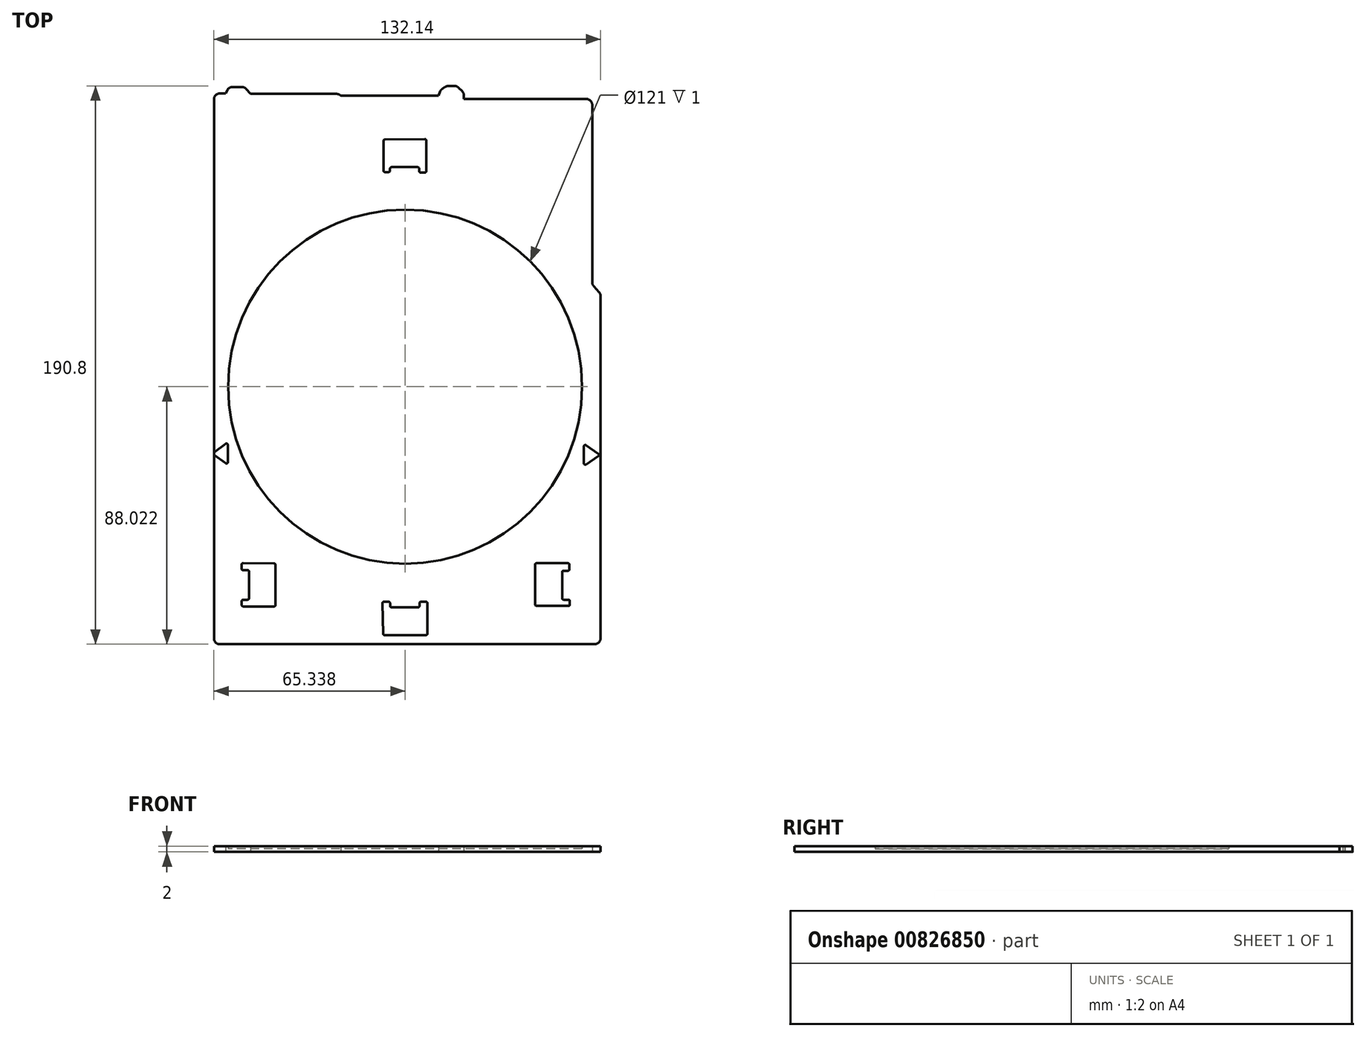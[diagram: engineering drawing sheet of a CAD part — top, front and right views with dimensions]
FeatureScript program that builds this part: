
annotation { "Feature Type Name" : "Feature", "Feature Type Description" : "" }
export const myFeature = defineFeature(function(context is Context, id is Id, definition is map)
    precondition{}
    {
        {
            var Q0;
            Q0=qCreatedBy(makeId("Top.planeOp"),FACE);
            var sketch = newSketch(context, id + "F0", { "sketchPlane" : qUnion([Q0])});
            skCircle(sketch, "E0", {"center": v(8.35, 24.71) * mm, "radius": 60.5 * mm, "construction": true});
            skLineSegment(sketch, "E1", {"start": v(-54.99, 124.93) * mm, "end": v(-53.03, 124.93) * mm});
            skLineSegment(sketch, "E2", {"start": v(-53.03, 124.93) * mm, "end": v(-52.4, 126.1) * mm});
            skLineSegment(sketch, "E3", {"start": v(-50.64, 127.15) * mm, "end": v(-47.47, 127.15) * mm});
            skLineSegment(sketch, "E4", {"start": v(-45.95, 126.45) * mm, "end": v(-44.5, 124.76) * mm});
            skLineSegment(sketch, "E5", {"start": v(-44.5, 124.76) * mm, "end": v(-15.05, 124.76) * mm});
            skLineSegment(sketch, "E6", {"start": v(-13.78, 124.3) * mm, "end": v(-13.6, 124.17) * mm});
            skLineSegment(sketch, "E7", {"start": v(-13.6, 124.17) * mm, "end": v(19.8, 124.17) * mm});
            skLineSegment(sketch, "E8", {"start": v(19.8, 124.17) * mm, "end": v(20.34, 125.59) * mm});
            skLineSegment(sketch, "E9", {"start": v(21.14, 126.57) * mm, "end": v(22.08, 127.18) * mm});
            skLineSegment(sketch, "E10", {"start": v(23.16, 127.5) * mm, "end": v(25.23, 127.5) * mm});
            skLineSegment(sketch, "E11", {"start": v(26.66, 126.9) * mm, "end": v(27.88, 125.64) * mm});
            skLineSegment(sketch, "E12", {"start": v(28.46, 124.24) * mm, "end": v(28.46, 123.02) * mm});
            skLineSegment(sketch, "E13", {"start": v(28.46, 123.02) * mm, "end": v(70.31, 123.02) * mm});
            skLineSegment(sketch, "E14", {"start": v(72.31, 121.02) * mm, "end": v(72.31, 60.41) * mm});
            skLineSegment(sketch, "E15", {"start": v(72.83, 59.08) * mm, "end": v(74.64, 57.06) * mm});
            skLineSegment(sketch, "E16", {"start": v(75.15, 55.72) * mm, "end": v(75.15, -61.3) * mm});
            skLineSegment(sketch, "E17", {"start": v(73.15, -63.3) * mm, "end": v(-54.99, -63.3) * mm});
            skLineSegment(sketch, "E18", {"start": v(-56.99, -61.3) * mm, "end": v(-56.99, 122.93) * mm});
            skPoint(sketch, "E19.visualSharp", {"position": v(-56.99, 124.93) * mm});
            skArc(sketch, "E19.filletArc", {"start": v(-54.99, 124.93) * mm, "mid": v(-56.4, 124.35) * mm, "end": v(-56.99, 122.93) * mm});
            skPoint(sketch, "E20.visualSharp", {"position": v(72.31, 123.02) * mm});
            skArc(sketch, "E20.filletArc", {"start": v(72.31, 121.02) * mm, "mid": v(71.73, 122.43) * mm, "end": v(70.31, 123.02) * mm});
            skPoint(sketch, "E21.visualSharp", {"position": v(-51.83, 127.15) * mm});
            skArc(sketch, "E21.filletArc", {"start": v(-50.64, 127.15) * mm, "mid": v(-51.67, 126.87) * mm, "end": v(-52.4, 126.1) * mm});
            skPoint(sketch, "E22.visualSharp", {"position": v(-46.55, 127.15) * mm});
            skArc(sketch, "E22.filletArc", {"start": v(-45.95, 126.45) * mm, "mid": v(-46.63, 126.97) * mm, "end": v(-47.47, 127.15) * mm});
            skPoint(sketch, "E23.visualSharp", {"position": v(22.58, 127.5) * mm});
            skArc(sketch, "E23.filletArc", {"start": v(23.16, 127.5) * mm, "mid": v(22.6, 127.41) * mm, "end": v(22.08, 127.18) * mm});
            skPoint(sketch, "E24.visualSharp", {"position": v(20.57, 126.21) * mm});
            skArc(sketch, "E24.filletArc", {"start": v(21.14, 126.57) * mm, "mid": v(20.66, 126.14) * mm, "end": v(20.34, 125.59) * mm});
            skPoint(sketch, "E25.visualSharp", {"position": v(26.07, 127.5) * mm});
            skArc(sketch, "E25.filletArc", {"start": v(26.66, 126.9) * mm, "mid": v(26, 127.33) * mm, "end": v(25.23, 127.5) * mm});
            skPoint(sketch, "E26.visualSharp", {"position": v(28.46, 125.06) * mm});
            skArc(sketch, "E26.filletArc", {"start": v(28.46, 124.24) * mm, "mid": v(28.3, 125) * mm, "end": v(27.88, 125.64) * mm});
            skPoint(sketch, "E27.visualSharp", {"position": v(75.15, 56.49) * mm});
            skArc(sketch, "E27.filletArc", {"start": v(75.15, 55.72) * mm, "mid": v(75.02, 56.44) * mm, "end": v(74.64, 57.06) * mm});
            skPoint(sketch, "E28.visualSharp", {"position": v(72.31, 59.65) * mm});
            skArc(sketch, "E28.filletArc", {"start": v(72.31, 60.41) * mm, "mid": v(72.45, 59.7) * mm, "end": v(72.83, 59.08) * mm});
            skPoint(sketch, "E29.visualSharp", {"position": v(-14.33, 124.76) * mm});
            skArc(sketch, "E29.filletArc", {"start": v(-13.78, 124.3) * mm, "mid": v(-14.37, 124.65) * mm, "end": v(-15.05, 124.76) * mm});
            skPoint(sketch, "E30.visualSharp", {"position": v(75.15, -63.3) * mm});
            skArc(sketch, "E30.filletArc", {"start": v(73.15, -63.3) * mm, "mid": v(74.57, -62.72) * mm, "end": v(75.15, -61.3) * mm});
            skPoint(sketch, "E31.visualSharp", {"position": v(-56.99, -63.3) * mm});
            skArc(sketch, "E31.filletArc", {"start": v(-56.99, -61.3) * mm, "mid": v(-56.4, -62.72) * mm, "end": v(-54.99, -63.3) * mm});
            skSolve(sketch);
        }
        {
            var Q0;
            Q0 = qSketchRegion(id + "F0", true);
            extrude(context, id + "F1", {"entities" : qUnion([Q0]), "depth" : 1 * mm, "offsetDistance" : 25 * mm});
        }
        {
            var Q0;
            Q0=makeQuery(id+"F1.opExtrude","CAP_FACE",FACE,{"disambiguationData":[OSD([sQuery(id+"F0.wireOp",EDGE,"E1"),sQuery(id+"F0.wireOp",EDGE,"E2"),sQuery(id+"F0.wireOp",EDGE,"E3"),sQuery(id+"F0.wireOp",EDGE,"E4"),sQuery(id+"F0.wireOp",EDGE,"E5"),sQuery(id+"F0.wireOp",EDGE,"E6"),sQuery(id+"F0.wireOp",EDGE,"E7"),sQuery(id+"F0.wireOp",EDGE,"E8"),sQuery(id+"F0.wireOp",EDGE,"E9"),sQuery(id+"F0.wireOp",EDGE,"E10"),sQuery(id+"F0.wireOp",EDGE,"E11"),sQuery(id+"F0.wireOp",EDGE,"E12"),sQuery(id+"F0.wireOp",EDGE,"E13"),sQuery(id+"F0.wireOp",EDGE,"E14"),sQuery(id+"F0.wireOp",EDGE,"E15"),sQuery(id+"F0.wireOp",EDGE,"E16"),sQuery(id+"F0.wireOp",EDGE,"E17"),sQuery(id+"F0.wireOp",EDGE,"E18"),sQuery(id+"F0.wireOp",EDGE,"E19.filletArc"),sQuery(id+"F0.wireOp",EDGE,"E20.filletArc"),sQuery(id+"F0.wireOp",EDGE,"E21.filletArc"),sQuery(id+"F0.wireOp",EDGE,"E22.filletArc"),sQuery(id+"F0.wireOp",EDGE,"E23.filletArc"),sQuery(id+"F0.wireOp",EDGE,"E24.filletArc"),sQuery(id+"F0.wireOp",EDGE,"E25.filletArc"),sQuery(id+"F0.wireOp",EDGE,"E26.filletArc"),sQuery(id+"F0.wireOp",EDGE,"E27.filletArc"),sQuery(id+"F0.wireOp",EDGE,"E28.filletArc"),sQuery(id+"F0.wireOp",EDGE,"E29.filletArc"),sQuery(id+"F0.wireOp",EDGE,"E30.filletArc"),sQuery(id+"F0.wireOp",EDGE,"E31.filletArc")])],"isStart":false});
            var sketch = newSketch(context, id + "F2", { "sketchPlane" : qUnion([Q0])});
            skLineSegment(sketch, "E32.0", {"start": v(-44.5, 124.76) * mm, "end": v(-15.05, 124.76) * mm});
            skLineSegment(sketch, "E32.1", {"start": v(75.15, 55.72) * mm, "end": v(75.15, -61.3) * mm});
            skLineSegment(sketch, "E32.2", {"start": v(-56.99, -61.3) * mm, "end": v(-56.99, 122.93) * mm});
            skLineSegment(sketch, "E32.3", {"start": v(28.46, 123.02) * mm, "end": v(70.31, 123.02) * mm});
            skLineSegment(sketch, "E32.4", {"start": v(73.15, -63.3) * mm, "end": v(-54.99, -63.3) * mm});
            skLineSegment(sketch, "E32.5", {"start": v(-13.6, 124.17) * mm, "end": v(19.8, 124.17) * mm});
            skLineSegment(sketch, "E32.6", {"start": v(72.31, 121.02) * mm, "end": v(72.31, 60.41) * mm});
            skCircle(sketch, "E32.7", {"center": v(8.35, 24.71) * mm, "radius": 60.5 * mm});
            skLineSegment(sketch, "E32.8", {"start": v(-56.99, -61.3) * mm, "end": v(-56.99, 122.93) * mm});
            skLineSegment(sketch, "E32.9", {"start": v(72.31, 121.02) * mm, "end": v(72.31, 60.41) * mm});
            skLineSegment(sketch, "E33.0", {"start": v(-50.64, 127.15) * mm, "end": v(-47.47, 127.15) * mm});
            skLineSegment(sketch, "E33.1", {"start": v(-45.95, 126.45) * mm, "end": v(-44.5, 124.76) * mm});
            skArc(sketch, "E33.2", {"start": v(-54.99, 124.93) * mm, "mid": v(-56.4, 124.35) * mm, "end": v(-56.99, 122.93) * mm});
            skLineSegment(sketch, "E33.3", {"start": v(-54.99, 124.93) * mm, "end": v(-53.03, 124.93) * mm});
            skArc(sketch, "E33.4", {"start": v(-50.64, 127.15) * mm, "mid": v(-51.67, 126.87) * mm, "end": v(-52.4, 126.1) * mm});
            skLineSegment(sketch, "E34.0", {"start": v(28.46, 124.24) * mm, "end": v(28.46, 123.02) * mm});
            skLineSegment(sketch, "E34.1", {"start": v(19.8, 124.17) * mm, "end": v(20.34, 125.59) * mm});
            skLineSegment(sketch, "E34.2", {"start": v(23.16, 127.5) * mm, "end": v(25.23, 127.5) * mm});
            skLineSegment(sketch, "E34.3", {"start": v(26.66, 126.9) * mm, "end": v(27.88, 125.64) * mm});
            skArc(sketch, "E34.4", {"start": v(21.14, 126.57) * mm, "mid": v(20.66, 126.14) * mm, "end": v(20.34, 125.59) * mm});
            skArc(sketch, "E34.5", {"start": v(26.66, 126.9) * mm, "mid": v(26, 127.33) * mm, "end": v(25.23, 127.5) * mm});
            skArc(sketch, "E34.6", {"start": v(28.46, 124.24) * mm, "mid": v(28.3, 125) * mm, "end": v(27.88, 125.64) * mm});
            skArc(sketch, "E35.0", {"start": v(72.31, 121.02) * mm, "mid": v(71.73, 122.43) * mm, "end": v(70.31, 123.02) * mm});
            skSolve(sketch);
        }
        {
            var Q0;
            Q0=makeQuery(id+"F2.imprint","IMPRINT",FACE,{"disambiguationData":[TD([[makeQuery(id+"F2.imprint","IMPRINT",EDGE,{"derivedFrom":sQuery(id+"F2.wireOp",EDGE,"E32.0")}),-1.0]])]});
            extrude(context, id + "F3", {"entities" : qUnion([Q0]), "operationType" : NewBodyOperationType.ADD, "depth" : 1 * mm, "offsetDistance" : 25 * mm});
        }
        {
            var Q0;
            Q0=makeQuery(id+"F3.opExtrude","CAP_FACE",FACE,{"disambiguationData":[OSD([sQuery(id+"F0.wireOp",EDGE,"E2"),sQuery(id+"F0.wireOp",EDGE,"E6"),sQuery(id+"F0.wireOp",EDGE,"E9"),sQuery(id+"F0.wireOp",EDGE,"E15"),sQuery(id+"F0.wireOp",EDGE,"E22.filletArc"),sQuery(id+"F0.wireOp",EDGE,"E23.filletArc"),sQuery(id+"F0.wireOp",EDGE,"E27.filletArc"),sQuery(id+"F0.wireOp",EDGE,"E28.filletArc"),sQuery(id+"F0.wireOp",EDGE,"E29.filletArc"),sQuery(id+"F0.wireOp",EDGE,"E30.filletArc"),sQuery(id+"F0.wireOp",EDGE,"E31.filletArc"),sQuery(id+"F2.wireOp",EDGE,"E32.0"),sQuery(id+"F2.wireOp",EDGE,"E32.1"),sQuery(id+"F2.wireOp",EDGE,"E32.3"),sQuery(id+"F2.wireOp",EDGE,"E32.4"),sQuery(id+"F2.wireOp",EDGE,"E32.5"),sQuery(id+"F2.wireOp",EDGE,"E32.7"),sQuery(id+"F2.wireOp",EDGE,"E32.8"),sQuery(id+"F2.wireOp",EDGE,"E32.9"),sQuery(id+"F2.wireOp",EDGE,"E33.0"),sQuery(id+"F2.wireOp",EDGE,"E33.1"),sQuery(id+"F2.wireOp",EDGE,"E33.2"),sQuery(id+"F2.wireOp",EDGE,"E33.3"),sQuery(id+"F2.wireOp",EDGE,"E33.4"),sQuery(id+"F2.wireOp",EDGE,"E34.0"),sQuery(id+"F2.wireOp",EDGE,"E34.1"),sQuery(id+"F2.wireOp",EDGE,"E34.2"),sQuery(id+"F2.wireOp",EDGE,"E34.3"),sQuery(id+"F2.wireOp",EDGE,"E34.4"),sQuery(id+"F2.wireOp",EDGE,"E34.5"),sQuery(id+"F2.wireOp",EDGE,"E34.6"),sQuery(id+"F2.wireOp",EDGE,"E35.0")])],"isStart":false});
            var sketch = newSketch(context, id + "F4", { "sketchPlane" : qUnion([Q0])});
            skLineSegment(sketch, "E36", {"start": v(-47.55, -36.14) * mm, "end": v(-47.55, -37.5) * mm});
            skLineSegment(sketch, "E37", {"start": v(-47.05, -38) * mm, "end": v(-45.5, -38) * mm});
            skLineSegment(sketch, "E38", {"start": v(-45, -38.5) * mm, "end": v(-45, -47.6) * mm});
            skLineSegment(sketch, "E39", {"start": v(-45.5, -48.1) * mm, "end": v(-47, -48.1) * mm});
            skLineSegment(sketch, "E40", {"start": v(-47.5, -48.6) * mm, "end": v(-47.5, -49.9) * mm});
            skLineSegment(sketch, "E41", {"start": v(-47, -50.4) * mm, "end": v(-36.45, -50.4) * mm});
            skLineSegment(sketch, "E42", {"start": v(-35.95, -49.9) * mm, "end": v(-35.95, -36.22) * mm});
            skLineSegment(sketch, "E43", {"start": v(-36.44, -35.72) * mm, "end": v(-47.05, -35.64) * mm});
            skLineSegment(sketch, "E44", {"start": v(1.1, -48.8) * mm, "end": v(2.72, -48.8) * mm});
            skLineSegment(sketch, "E45", {"start": v(3.22, -49.3) * mm, "end": v(3.22, -50.21) * mm});
            skLineSegment(sketch, "E46", {"start": v(3.72, -50.71) * mm, "end": v(12.76, -50.71) * mm});
            skLineSegment(sketch, "E47", {"start": v(13.26, -50.21) * mm, "end": v(13.26, -49.3) * mm});
            skLineSegment(sketch, "E48", {"start": v(13.76, -48.8) * mm, "end": v(15.47, -48.8) * mm});
            skLineSegment(sketch, "E49", {"start": v(15.97, -49.3) * mm, "end": v(15.97, -59.7) * mm});
            skLineSegment(sketch, "E50", {"start": v(15.47, -60.2) * mm, "end": v(1.31, -60.2) * mm});
            skLineSegment(sketch, "E51", {"start": v(0.82, -59.7) * mm, "end": v(0.6, -49.3) * mm});
            skLineSegment(sketch, "E52", {"start": v(52.8, -36.13) * mm, "end": v(52.8, -49.73) * mm});
            skLineSegment(sketch, "E53", {"start": v(53.3, -50.23) * mm, "end": v(64.17, -50.23) * mm});
            skLineSegment(sketch, "E54", {"start": v(64.67, -49.73) * mm, "end": v(64.67, -48.6) * mm});
            skLineSegment(sketch, "E55", {"start": v(64.17, -48.1) * mm, "end": v(62.55, -48.1) * mm});
            skLineSegment(sketch, "E56", {"start": v(62.05, -47.6) * mm, "end": v(62.05, -38.7) * mm});
            skLineSegment(sketch, "E57", {"start": v(62.55, -38.2) * mm, "end": v(64.02, -38.2) * mm});
            skLineSegment(sketch, "E58", {"start": v(64.52, -37.7) * mm, "end": v(64.52, -36.13) * mm});
            skLineSegment(sketch, "E59", {"start": v(64.02, -35.63) * mm, "end": v(53.3, -35.63) * mm});
            skLineSegment(sketch, "E60", {"start": v(69.46, 4.28) * mm, "end": v(69.46, -1.48) * mm});
            skLineSegment(sketch, "E61", {"start": v(70.24, -1.9) * mm, "end": v(74.42, 0.95) * mm});
            skLineSegment(sketch, "E62", {"start": v(74.42, 1.77) * mm, "end": v(70.25, 4.69) * mm});
            skLineSegment(sketch, "E63", {"start": v(-56.95, 2.2) * mm, "end": v(-53.04, 5.19) * mm});
            skLineSegment(sketch, "E64", {"start": v(-52.24, 4.79) * mm, "end": v(-52.24, -1.08) * mm});
            skLineSegment(sketch, "E65", {"start": v(-53.04, -1.48) * mm, "end": v(-56.95, 1.4) * mm});
            skLineSegment(sketch, "E66", {"start": v(0.97, 108.72) * mm, "end": v(0.97, 98.56) * mm});
            skLineSegment(sketch, "E67", {"start": v(1.47, 98.06) * mm, "end": v(2.7, 98.06) * mm});
            skLineSegment(sketch, "E68", {"start": v(3.2, 98.56) * mm, "end": v(3.2, 99.23) * mm});
            skLineSegment(sketch, "E69", {"start": v(3.7, 99.73) * mm, "end": v(12.67, 99.73) * mm});
            skLineSegment(sketch, "E70", {"start": v(13.17, 99.23) * mm, "end": v(13.17, 98.4) * mm});
            skLineSegment(sketch, "E71", {"start": v(13.67, 97.9) * mm, "end": v(15.14, 97.9) * mm});
            skLineSegment(sketch, "E72", {"start": v(15.64, 98.4) * mm, "end": v(15.64, 108.8) * mm});
            skLineSegment(sketch, "E73", {"start": v(15.14, 109.3) * mm, "end": v(1.47, 109.22) * mm});
            skPoint(sketch, "E74.visualSharp", {"position": v(0.97, 109.22) * mm});
            skArc(sketch, "E74.filletArc", {"start": v(1.47, 109.22) * mm, "mid": v(1.11, 109.08) * mm, "end": v(0.97, 108.72) * mm});
            skPoint(sketch, "E75.visualSharp", {"position": v(15.64, 109.3) * mm});
            skArc(sketch, "E75.filletArc", {"start": v(15.64, 108.8) * mm, "mid": v(15.5, 109.15) * mm, "end": v(15.14, 109.3) * mm});
            skPoint(sketch, "E76.visualSharp", {"position": v(15.64, 97.9) * mm});
            skArc(sketch, "E76.filletArc", {"start": v(15.14, 97.9) * mm, "mid": v(15.5, 98.05) * mm, "end": v(15.64, 98.4) * mm});
            skPoint(sketch, "E77.visualSharp", {"position": v(13.17, 99.73) * mm});
            skArc(sketch, "E77.filletArc", {"start": v(13.17, 99.23) * mm, "mid": v(13.02, 99.59) * mm, "end": v(12.67, 99.73) * mm});
            skPoint(sketch, "E78.visualSharp", {"position": v(3.2, 99.73) * mm});
            skArc(sketch, "E78.filletArc", {"start": v(3.7, 99.73) * mm, "mid": v(3.35, 99.59) * mm, "end": v(3.2, 99.23) * mm});
            skPoint(sketch, "E79.visualSharp", {"position": v(3.2, 98.06) * mm});
            skArc(sketch, "E79.filletArc", {"start": v(2.7, 98.06) * mm, "mid": v(3.06, 98.2) * mm, "end": v(3.2, 98.56) * mm});
            skPoint(sketch, "E80.visualSharp", {"position": v(0.97, 98.06) * mm});
            skArc(sketch, "E80.filletArc", {"start": v(0.97, 98.56) * mm, "mid": v(1.12, 98.2) * mm, "end": v(1.47, 98.06) * mm});
            skPoint(sketch, "E81.visualSharp", {"position": v(13.17, 97.9) * mm});
            skArc(sketch, "E81.filletArc", {"start": v(13.17, 98.4) * mm, "mid": v(13.31, 98.05) * mm, "end": v(13.67, 97.9) * mm});
            skPoint(sketch, "E82.visualSharp", {"position": v(75.01, 1.36) * mm});
            skArc(sketch, "E82.filletArc", {"start": v(74.42, 0.95) * mm, "mid": v(74.63, 1.36) * mm, "end": v(74.42, 1.77) * mm});
            skPoint(sketch, "E83.visualSharp", {"position": v(69.46, 5.23) * mm});
            skArc(sketch, "E83.filletArc", {"start": v(70.25, 4.69) * mm, "mid": v(69.73, 4.72) * mm, "end": v(69.46, 4.28) * mm});
            skPoint(sketch, "E84.visualSharp", {"position": v(69.46, -2.43) * mm});
            skArc(sketch, "E84.filletArc", {"start": v(69.46, -1.48) * mm, "mid": v(69.73, -1.93) * mm, "end": v(70.24, -1.9) * mm});
            skPoint(sketch, "E85.visualSharp", {"position": v(-52.24, 5.8) * mm});
            skArc(sketch, "E85.filletArc", {"start": v(-52.24, 4.79) * mm, "mid": v(-52.52, 5.24) * mm, "end": v(-53.04, 5.19) * mm});
            skPoint(sketch, "E86.visualSharp", {"position": v(-52.24, -2.07) * mm});
            skArc(sketch, "E86.filletArc", {"start": v(-53.04, -1.48) * mm, "mid": v(-52.51, -1.53) * mm, "end": v(-52.24, -1.08) * mm});
            skPoint(sketch, "E87.visualSharp", {"position": v(-57.48, 1.8) * mm});
            skArc(sketch, "E87.filletArc", {"start": v(-56.95, 2.2) * mm, "mid": v(-57.15, 1.8) * mm, "end": v(-56.95, 1.4) * mm});
            skPoint(sketch, "E88.visualSharp", {"position": v(-47.55, -35.63) * mm});
            skArc(sketch, "E88.filletArc", {"start": v(-47.05, -35.64) * mm, "mid": v(-47.4, -35.78) * mm, "end": v(-47.55, -36.14) * mm});
            skPoint(sketch, "E89.visualSharp", {"position": v(-35.95, -35.72) * mm});
            skArc(sketch, "E89.filletArc", {"start": v(-35.95, -36.22) * mm, "mid": v(-36.1, -35.87) * mm, "end": v(-36.44, -35.72) * mm});
            skPoint(sketch, "E90.visualSharp", {"position": v(-47.55, -38) * mm});
            skArc(sketch, "E90.filletArc", {"start": v(-47.55, -37.5) * mm, "mid": v(-47.4, -37.86) * mm, "end": v(-47.05, -38) * mm});
            skPoint(sketch, "E91.visualSharp", {"position": v(-45, -38) * mm});
            skArc(sketch, "E91.filletArc", {"start": v(-45, -38.5) * mm, "mid": v(-45.14, -38.15) * mm, "end": v(-45.5, -38) * mm});
            skPoint(sketch, "E92.visualSharp", {"position": v(-45, -48.1) * mm});
            skArc(sketch, "E92.filletArc", {"start": v(-45.5, -48.1) * mm, "mid": v(-45.14, -47.95) * mm, "end": v(-45, -47.6) * mm});
            skPoint(sketch, "E93.visualSharp", {"position": v(-47.5, -48.1) * mm});
            skArc(sketch, "E93.filletArc", {"start": v(-47, -48.1) * mm, "mid": v(-47.36, -48.25) * mm, "end": v(-47.5, -48.6) * mm});
            skPoint(sketch, "E94.visualSharp", {"position": v(-47.5, -50.4) * mm});
            skArc(sketch, "E94.filletArc", {"start": v(-47.5, -49.9) * mm, "mid": v(-47.36, -50.25) * mm, "end": v(-47, -50.4) * mm});
            skPoint(sketch, "E95.visualSharp", {"position": v(-35.95, -50.4) * mm});
            skArc(sketch, "E95.filletArc", {"start": v(-36.45, -50.4) * mm, "mid": v(-36.1, -50.25) * mm, "end": v(-35.95, -49.9) * mm});
            skPoint(sketch, "E96.visualSharp", {"position": v(0.59, -48.8) * mm});
            skArc(sketch, "E96.filletArc", {"start": v(1.1, -48.8) * mm, "mid": v(0.74, -48.95) * mm, "end": v(0.6, -49.3) * mm});
            skPoint(sketch, "E97.visualSharp", {"position": v(3.22, -48.8) * mm});
            skArc(sketch, "E97.filletArc", {"start": v(3.22, -49.3) * mm, "mid": v(3.07, -48.95) * mm, "end": v(2.72, -48.8) * mm});
            skPoint(sketch, "E98.visualSharp", {"position": v(3.22, -50.71) * mm});
            skArc(sketch, "E98.filletArc", {"start": v(3.22, -50.21) * mm, "mid": v(3.36, -50.57) * mm, "end": v(3.72, -50.71) * mm});
            skPoint(sketch, "E99.visualSharp", {"position": v(13.26, -50.71) * mm});
            skArc(sketch, "E99.filletArc", {"start": v(12.76, -50.71) * mm, "mid": v(13.12, -50.57) * mm, "end": v(13.26, -50.21) * mm});
            skPoint(sketch, "E100.visualSharp", {"position": v(13.26, -48.8) * mm});
            skArc(sketch, "E100.filletArc", {"start": v(13.76, -48.8) * mm, "mid": v(13.4, -48.95) * mm, "end": v(13.26, -49.3) * mm});
            skPoint(sketch, "E101.visualSharp", {"position": v(15.97, -48.8) * mm});
            skArc(sketch, "E101.filletArc", {"start": v(15.97, -49.3) * mm, "mid": v(15.83, -48.95) * mm, "end": v(15.47, -48.8) * mm});
            skPoint(sketch, "E102.visualSharp", {"position": v(15.97, -60.2) * mm});
            skArc(sketch, "E102.filletArc", {"start": v(15.47, -60.2) * mm, "mid": v(15.83, -60.05) * mm, "end": v(15.97, -59.7) * mm});
            skPoint(sketch, "E103.visualSharp", {"position": v(0.83, -60.2) * mm});
            skArc(sketch, "E103.filletArc", {"start": v(0.82, -59.7) * mm, "mid": v(0.97, -60.06) * mm, "end": v(1.31, -60.2) * mm});
            skPoint(sketch, "E104.visualSharp", {"position": v(52.8, -50.23) * mm});
            skArc(sketch, "E104.filletArc", {"start": v(52.8, -49.73) * mm, "mid": v(52.95, -50.09) * mm, "end": v(53.3, -50.23) * mm});
            skPoint(sketch, "E105.visualSharp", {"position": v(52.8, -35.63) * mm});
            skArc(sketch, "E105.filletArc", {"start": v(53.3, -35.63) * mm, "mid": v(52.95, -35.78) * mm, "end": v(52.8, -36.13) * mm});
            skPoint(sketch, "E106.visualSharp", {"position": v(64.52, -35.63) * mm});
            skArc(sketch, "E106.filletArc", {"start": v(64.52, -36.13) * mm, "mid": v(64.38, -35.78) * mm, "end": v(64.02, -35.63) * mm});
            skPoint(sketch, "E107.visualSharp", {"position": v(64.52, -38.2) * mm});
            skArc(sketch, "E107.filletArc", {"start": v(64.02, -38.2) * mm, "mid": v(64.38, -38.05) * mm, "end": v(64.52, -37.7) * mm});
            skPoint(sketch, "E108.visualSharp", {"position": v(62.05, -38.2) * mm});
            skArc(sketch, "E108.filletArc", {"start": v(62.55, -38.2) * mm, "mid": v(62.2, -38.34) * mm, "end": v(62.05, -38.7) * mm});
            skPoint(sketch, "E109.visualSharp", {"position": v(62.05, -48.1) * mm});
            skArc(sketch, "E109.filletArc", {"start": v(62.05, -47.6) * mm, "mid": v(62.2, -47.95) * mm, "end": v(62.55, -48.1) * mm});
            skPoint(sketch, "E110.visualSharp", {"position": v(64.67, -48.1) * mm});
            skArc(sketch, "E110.filletArc", {"start": v(64.67, -48.6) * mm, "mid": v(64.52, -48.25) * mm, "end": v(64.17, -48.1) * mm});
            skPoint(sketch, "E111.visualSharp", {"position": v(64.67, -50.23) * mm});
            skArc(sketch, "E111.filletArc", {"start": v(64.17, -50.23) * mm, "mid": v(64.52, -50.09) * mm, "end": v(64.67, -49.73) * mm});
            skSolve(sketch);
        }
        {
            var Q0;
            Q0 = qSketchRegion(id + "F4", true);
            extrude(context, id + "F5", {"entities" : qUnion([Q0]), "operationType" : NewBodyOperationType.REMOVE, "oppositeDirection" : true, "depth" : 0.2 * mm, "offsetDistance" : 25 * mm});
        }
    });
